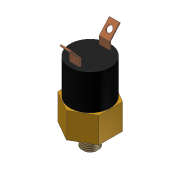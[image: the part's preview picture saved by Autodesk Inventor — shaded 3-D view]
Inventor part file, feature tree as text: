
AUTODESK INVENTOR PART (.ipt)
format: ipt  version: 2014 SP1 (Build 180222100, 222)  size: 161,280 bytes
history: native  units: mm (DEFAULTED — no unit token found)
features: extrude x6, sketch x6, projected_geometry x4, mirror x1, thread x1, chamfer x1, fillet x1
ambient origin geometry x8: Origin, YZ Plane, XZ Plane, XY Plane, X Axis, Y Axis, Z Axis, Center Point
bodies: Solid1 (feature_tree)
feature tree (20):
  extrude  "Extrusion1"  Depth=15.875mm TaperAngle=0.0deg
  extrude  "Extrusion2"  Depth=11.049mm TaperAngle=0.0deg
  extrude  "Extrusion3"  Depth=19.9898mm TaperAngle=0.0deg
  extrude  "Extrusion4"  Depth=21.971mm TaperAngle=0.0deg
  extrude  "Extrusion5"  Depth=0.762mm
  extrude  "Extrusion6"  Depth=3.175mm
  mirror  "Mirror1"
  thread  "Thread1"  [1 undecoded]
  chamfer  "Chamfer1"  Distance=6.35mm
  fillet  "Fillet1"  Radius=6.35mm
  sketch  "Sketch1"  dims[d0=25.4mm d1=15.875mm d2=0.0mm]
  sketch  "Sketch2"  dims[d3=10.16mm d4=11.049mm d5=0.0mm]
  projected_geometry  "Projected Loop1"
  sketch  "Sketch3"  dims[d6=3.175mm d7=19.9898mm d8=0.0mm]
  sketch  "Sketch4"  dims[d9=24.765mm d10=21.971mm d11=0.0mm]
  projected_geometry  "Projected Loop2"
  sketch  "Sketch5"  dims[d12=19.05mm d13=0.762mm]
  projected_geometry  "Projected Loop3"
  sketch  "Sketch6"  dims[d14=0.762mm d15=4.699mm d17=9.398mm d18=6.35mm d19=0.0mm d20=6.35mm d21=0.0mm d22=25.4mm d23=0.0mm d24=1.0mm d25=3.175mm d26=45.0deg d27=3.175mm]
  projected_geometry  "Projected Loop4"
note: 1 required parameter value undecoded (feature->parameter linkage not recoverable at this tier; creation-order binding heuristic only, values carry confidence <= 0.55)
